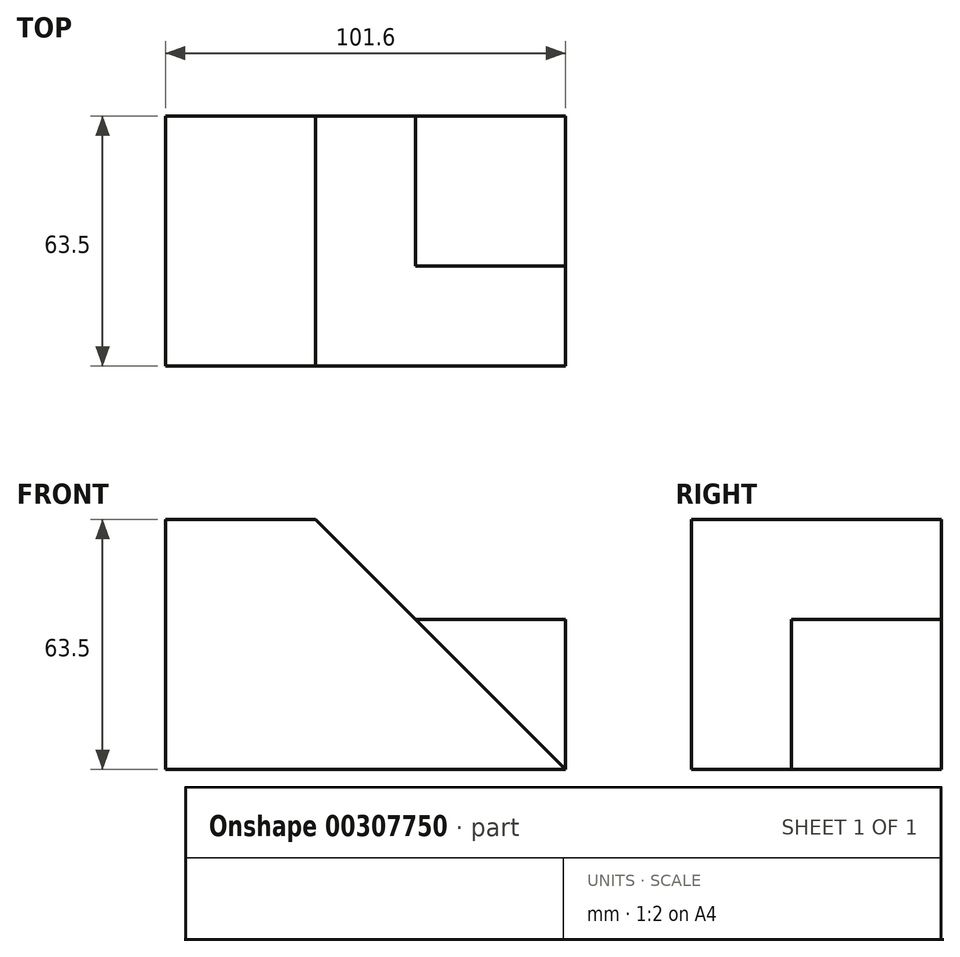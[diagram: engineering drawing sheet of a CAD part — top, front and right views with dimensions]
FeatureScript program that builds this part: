
annotation { "Feature Type Name" : "Feature", "Feature Type Description" : "" }
export const myFeature = defineFeature(function(context is Context, id is Id, definition is map)
    precondition{}
    {
        {
            var Q0;
            Q0=qCreatedBy(makeId("Front.planeOp"),FACE);
            var sketch = newSketch(context, id + "F0", { "sketchPlane" : qUnion([Q0])});
            skLineSegment(sketch, "E0", {"start": v(-60.4, -68.67) * mm, "end": v(-60.4, -5.17) * mm});
            skLineSegment(sketch, "E1", {"start": v(-60.4, -5.17) * mm, "end": v(-22.3, -5.17) * mm});
            skLineSegment(sketch, "E2", {"start": v(-60.4, -68.67) * mm, "end": v(41.2, -68.67) * mm});
            skLineSegment(sketch, "E3", {"start": v(41.2, -68.67) * mm, "end": v(-22.3, -5.17) * mm});
            skSolve(sketch);
        }
        {
            var Q0;
            Q0 = qSketchRegion(id + "F0", true);
            var Q1;
            Q1=makeQuery(id+"F0.imprint","IMPRINT",FACE,{"disambiguationData":[TD([[makeQuery(id+"F0.imprint","IMPRINT",EDGE,{"derivedFrom":sQuery(id+"F0.wireOp",EDGE,"E0")}),-1.0]])]});
            extrude(context, id + "F1", {"entities" : qUnion([Q0, Q1]), "depth" : 63.5 * mm});
        }
        {
            var Q0;
            Q0=makeQuery(id+"F1.opExtrude","CAP_FACE",FACE,{"disambiguationData":[OSD([sQuery(id+"F0.wireOp",EDGE,"E0"),sQuery(id+"F0.wireOp",EDGE,"E1"),sQuery(id+"F0.wireOp",EDGE,"E2"),sQuery(id+"F0.wireOp",EDGE,"E3")])],"isStart":true});
            var sketch = newSketch(context, id + "F2", { "sketchPlane" : qUnion([Q0])});
            skLineSegment(sketch, "E4", {"start": v(-41.2, -68.67) * mm, "end": v(-3.1, -68.67) * mm});
            skLineSegment(sketch, "E5", {"start": v(-3.1, -68.67) * mm, "end": v(-3.1, -30.57) * mm});
            skLineSegment(sketch, "E6", {"start": v(-3.1, -30.57) * mm, "end": v(-41.2, -30.57) * mm});
            skLineSegment(sketch, "E7", {"start": v(-41.2, -30.57) * mm, "end": v(-41.2, -68.67) * mm});
            skSolve(sketch);
        }
        {
            var Q0;
            {var subQ0=sQuery(id+"F2.wireOp",EDGE,"E6");Q0=makeQuery(id+"F2.imprint","IMPRINT",FACE,{"disambiguationData":[TD([[makeQuery(id+"F2.imprint","IMPRINT",EDGE,{"derivedFrom":subQ0}),1.0]])]});}
            extrude(context, id + "F3", {"entities" : qUnion([Q0]), "operationType" : NewBodyOperationType.ADD, "oppositeDirection" : true, "depth" : 38.1 * mm});
        }
    });
